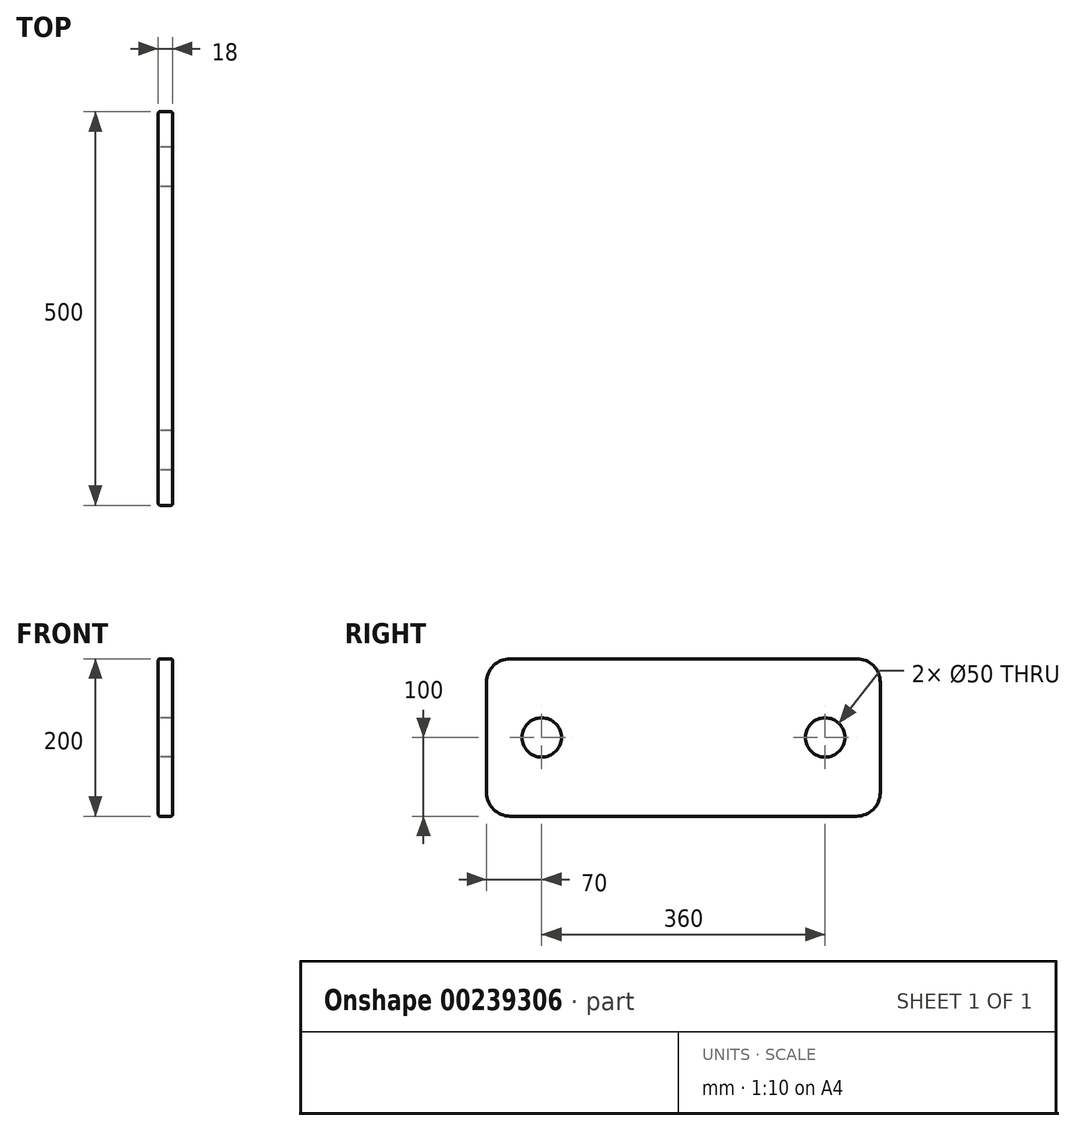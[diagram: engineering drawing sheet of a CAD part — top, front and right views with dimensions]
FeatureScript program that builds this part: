
annotation { "Feature Type Name" : "Feature", "Feature Type Description" : "" }
export const myFeature = defineFeature(function(context is Context, id is Id, definition is map)
    precondition{}
    {
        {
            var Q0;
            Q0=qCreatedBy(makeId("Right.planeOp"),FACE);
            var sketch = newSketch(context, id + "F0", { "sketchPlane" : qUnion([Q0])});
            skLineSegment(sketch, "E0.bottom", {"start": v(30, 0) * mm, "end": v(470, 0) * mm});
            skLineSegment(sketch, "E0.top", {"start": v(30, 200) * mm, "end": v(470, 200) * mm});
            skLineSegment(sketch, "E0.left", {"start": v(0, 30) * mm, "end": v(0, 170) * mm});
            skLineSegment(sketch, "E0.right", {"start": v(500, 30) * mm, "end": v(500, 170) * mm});
            skPoint(sketch, "E1.visualSharp", {"position": v(0, 200) * mm});
            skArc(sketch, "E1.filletArc", {"start": v(30, 200) * mm, "mid": v(8.79, 191.21) * mm, "end": v(0, 170) * mm});
            skPoint(sketch, "E2.visualSharp", {"position": v(500, 200) * mm});
            skArc(sketch, "E2.filletArc", {"start": v(500, 170) * mm, "mid": v(491.21, 191.21) * mm, "end": v(470, 200) * mm});
            skPoint(sketch, "E3.visualSharp", {"position": v(500, 0) * mm});
            skArc(sketch, "E3.filletArc", {"start": v(470, 0) * mm, "mid": v(491.21, 8.79) * mm, "end": v(500, 30) * mm});
            skPoint(sketch, "E4.visualSharp", {"position": v(0, 0) * mm});
            skArc(sketch, "E4.filletArc", {"start": v(0, 30) * mm, "mid": v(8.79, 8.79) * mm, "end": v(30, 0) * mm});
            skCircle(sketch, "E5", {"center": v(250, 275) * mm, "radius": 222.5 * mm, "construction": true});
            skLineSegment(sketch, "E6", {"start": v(0, 100) * mm, "end": v(500, 100) * mm, "construction": true});
            skLineSegment(sketch, "E7", {"start": v(250, 0) * mm, "end": v(250, 200) * mm, "construction": true});
            skCircle(sketch, "E8", {"center": v(70, 100) * mm, "radius": 25 * mm});
            skCircle(sketch, "E9.MirrorC", {"center": v(430, 100) * mm, "radius": 25 * mm});
            skLineSegment(sketch, "E10", {"start": v(250, 200) * mm, "end": v(250, 275) * mm});
            skSolve(sketch);
        }
        {
            var Q0;
            Q0=makeQuery(id+"F0.imprint","IMPRINT",FACE,{"disambiguationData":[TD([[makeQuery(id+"F0.imprint","IMPRINT",EDGE,{"derivedFrom":sQuery(id+"F0.wireOp",EDGE,"E0.bottom")}),1.0]])]});
            extrude(context, id + "F1", {"entities" : qUnion([Q0]), "depth" : 18 * mm});
        }
        {
            var Q0;
            Q0=makeQuery(id+"F1.opExtrude","CAP_EDGE",EDGE,{"disambiguationData":[OSD([sQuery(id+"F0.wireOp",EDGE,"E0.top")])],"isStart":true});
            var Q1;
            Q1=makeQuery(id+"F1.opExtrude","CAP_EDGE",EDGE,{"disambiguationData":[OSD([sQuery(id+"F0.wireOp",EDGE,"E0.top")])],"isStart":false});
            fillet(context, id + "F2", {"entities" : qUnion([Q0, Q1]), "radius" : 2 * mm, "tangentPropagation" : true, "allowEdgeOverflow" : false});
        }
    });
